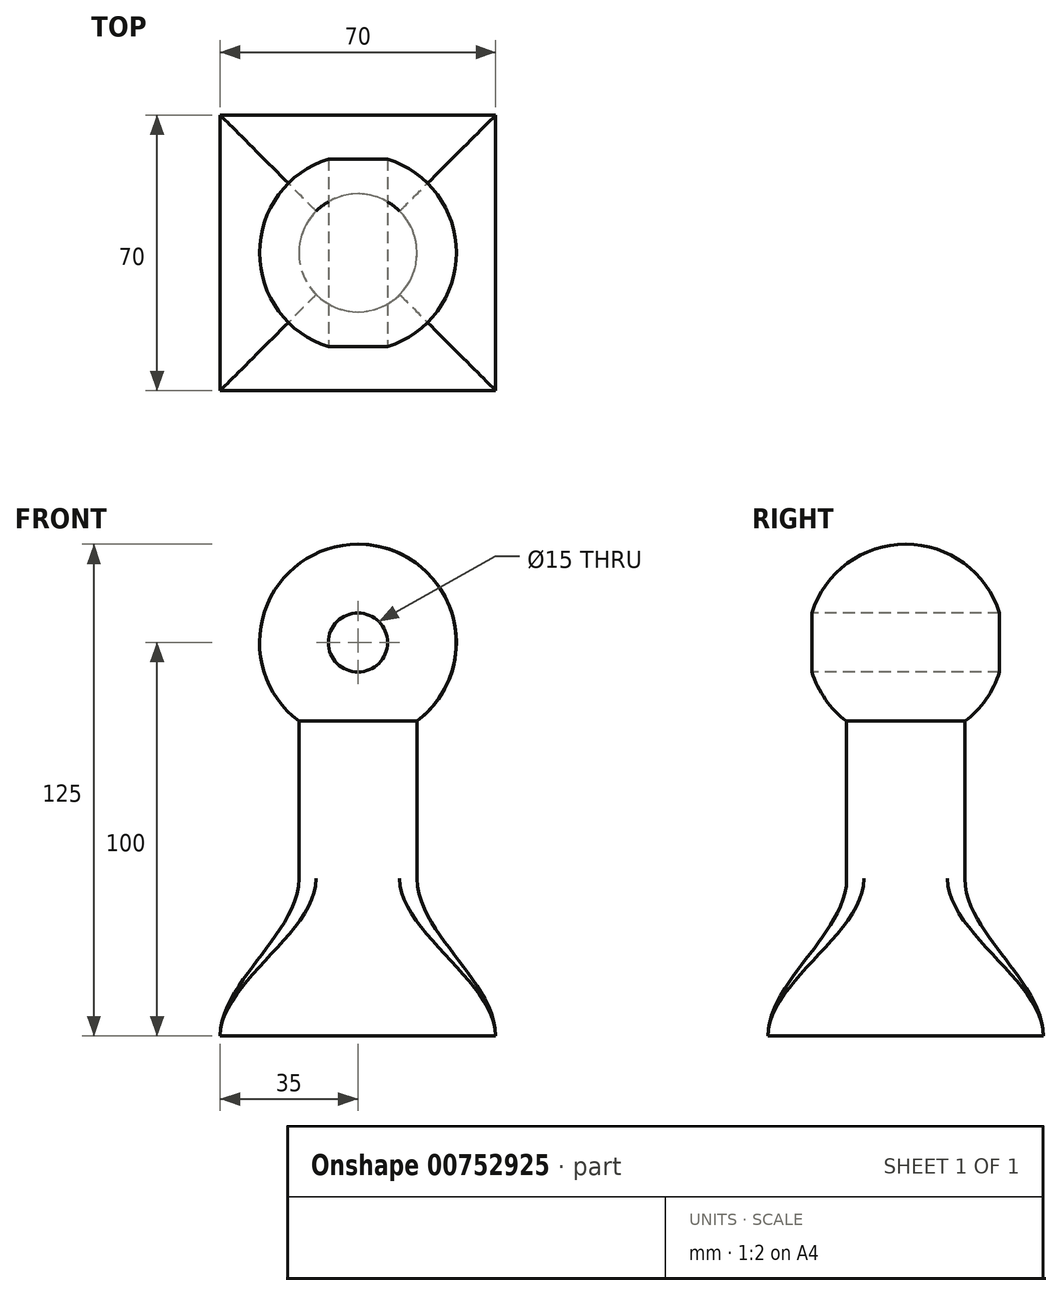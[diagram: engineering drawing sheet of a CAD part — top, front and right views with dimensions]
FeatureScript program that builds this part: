
annotation { "Feature Type Name" : "Feature", "Feature Type Description" : "" }
export const myFeature = defineFeature(function(context is Context, id is Id, definition is map)
    precondition{}
    {
        {
            var Q0;
            Q0=qCreatedBy(makeId("Front.planeOp"),FACE);
            var sketch = newSketch(context, id + "F0", { "sketchPlane" : qUnion([Q0])});
            skArc(sketch, "E0", {"start": v(0, -25) * mm, "mid": v(25, 0) * mm, "end": v(0, 25) * mm});
            skLineSegment(sketch, "E1.bottom", {"start": v(0, -25) * mm, "end": v(15, -25) * mm});
            skLineSegment(sketch, "E1.top", {"start": v(0, -60) * mm, "end": v(15, -60) * mm});
            skLineSegment(sketch, "E1.left", {"start": v(0, -25) * mm, "end": v(0, -60) * mm});
            skLineSegment(sketch, "E1.right", {"start": v(15, -25) * mm, "end": v(15, -60) * mm});
            skLineSegment(sketch, "E2", {"start": v(15, -25) * mm, "end": v(15, -20) * mm});
            skLineSegment(sketch, "E3", {"start": v(0, 25) * mm, "end": v(0, -25) * mm});
            skLineSegment(sketch, "E4", {"start": v(0, 25) * mm, "end": v(0, 55) * mm, "construction": true});
            skSolve(sketch);
        }
        {
            var Q0;
            {var subQ0=sQuery(id+"F0.wireOp",EDGE,"E3");Q0=makeQuery(id+"F0.imprint","IMPRINT",FACE,{"disambiguationData":[TD([[makeQuery(id+"F0.imprint","IMPRINT",EDGE,{"derivedFrom":subQ0}),1.0]])]});}
            var Q1;
            Q1=makeQuery(id+"F0.imprint","IMPRINT",FACE,{"disambiguationData":[TD([[makeQuery(id+"F0.imprint","IMPRINT",EDGE,{"derivedFrom":sQuery(id+"F0.wireOp",EDGE,"E1.bottom")}),-1.0]])]});
            var Q2;
            {var subQ0=sQuery(id+"F0.wireOp",EDGE,"E1.bottom");Q2=makeQuery(id+"F0.imprint","IMPRINT",FACE,{"disambiguationData":[TD([[makeQuery(id+"F0.imprint","IMPRINT",EDGE,{"derivedFrom":subQ0}),1.0]])]});}
            var Q3;
            Q3=sQuery(id+"F0.wireOp",EDGE,"E4");
            revolve(context, id + "F1", {"surfaceOperationType" : NewSurfaceOperationType.NEW, "entities" : qUnion([Q0, Q1, Q2]), "axis" : qUnion([Q3]), "revolveType" : RevolveType.FULL});
        }
        {
            var Q0;
            Q0=qCreatedBy(makeId("Front.planeOp"),FACE);
            var sketch = newSketch(context, id + "F2", { "sketchPlane" : qUnion([Q0])});
            skCircle(sketch, "E5", {"center": v(0, 0) * mm, "radius": 7.5 * mm});
            skSolve(sketch);
        }
        {
            var Q0;
            Q0 = qSketchRegion(id + "F2", true);
            extrude(context, id + "F3", {"entities" : qUnion([Q0]), "operationType" : NewBodyOperationType.REMOVE, "endBound" : BoundingType.THROUGH_ALL, "oppositeDirection" : true, "depth" : 25 * mm, "offsetDistance" : 25 * mm, "hasSecondDirection" : true, "secondDirectionBound" : SecondDirectionBoundingType.THROUGH_ALL, "secondDirectionOppositeDirection" : false, "secondDirectionDepth" : 25 * mm});
        }
        {
            var Q0;
            Q0=makeQuery(id+"F1.opRevolve","SWEPT_FACE",FACE,{"disambiguationData":[OSD([sQuery(id+"F0.wireOp",EDGE,"E1.top")])]});
            cPlane(context, id + "F4", {"entities" : qUnion([Q0]), "cplaneType" : CPlaneType.OFFSET, "offset" : 40 * mm, "width" : 150 * mm, "height" : 150 * mm});
        }
        {
            var Q0;
            Q0=qCreatedBy(id+"F4.planeOp",FACE);
            var sketch = newSketch(context, id + "F5", { "sketchPlane" : qUnion([Q0])});
            skLineSegment(sketch, "E6.bottom", {"start": v(-35, 35) * mm, "end": v(35, 35) * mm});
            skLineSegment(sketch, "E6.top", {"start": v(-35, -35) * mm, "end": v(35, -35) * mm});
            skLineSegment(sketch, "E6.left", {"start": v(-35, 35) * mm, "end": v(-35, -35) * mm});
            skLineSegment(sketch, "E6.right", {"start": v(35, 35) * mm, "end": v(35, -35) * mm});
            skPoint(sketch, "E6.middle", {"position": v(0, 0) * mm});
            skSolve(sketch);
        }
        {
            var Q0;
            Q0=makeQuery(id+"F1.opRevolve","SWEPT_FACE",FACE,{"disambiguationData":[OSD([sQuery(id+"F0.wireOp",EDGE,"E1.top")])]});
            var Q1;
            Q1=makeQuery(id+"F5.imprint","IMPRINT",FACE,{"disambiguationData":[TD([[makeQuery(id+"F5.imprint","IMPRINT",EDGE,{"derivedFrom":sQuery(id+"F5.wireOp",EDGE,"E6.bottom")}),-1.0]])]});
            loft(context, id + "F6", {"operationType" : NewBodyOperationType.ADD, "startCondition" : LoftEndDerivativeType.NORMAL_TO_PROFILE, "startMagnitude" : 1, "endCondition" : LoftEndDerivativeType.NORMAL_TO_PROFILE, "endMagnitude" : 1, "sheetProfilesArray" : [{ "sheetProfileEntities" : qUnion([Q0]) }, { "sheetProfileEntities" : qUnion([Q1]) }]});
        }
    });
